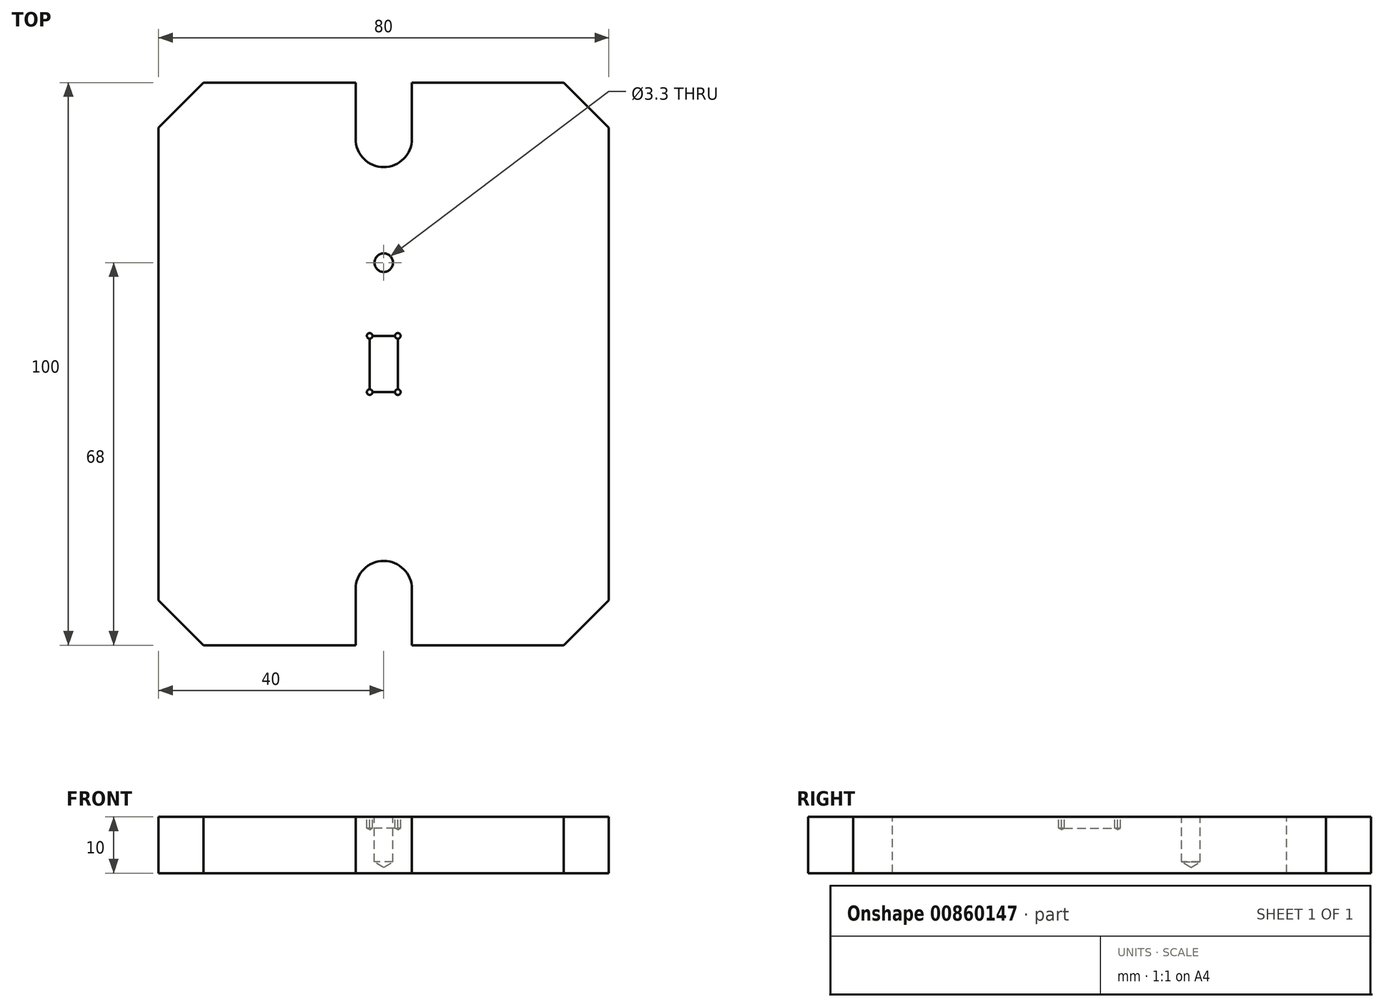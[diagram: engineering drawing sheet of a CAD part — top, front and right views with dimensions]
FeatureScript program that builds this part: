
annotation { "Feature Type Name" : "Feature", "Feature Type Description" : "" }
export const myFeature = defineFeature(function(context is Context, id is Id, definition is map)
    precondition{}
    {
        {
            var Q0;
            Q0=qCreatedBy(makeId("Top.planeOp"),FACE);
            var sketch = newSketch(context, id + "F0", { "sketchPlane" : qUnion([Q0])});
            skLineSegment(sketch, "E0.bottom", {"start": v(40, -50) * mm, "end": v(5, -50) * mm});
            skLineSegment(sketch, "E0.top", {"start": v(40, 50) * mm, "end": v(5, 50) * mm});
            skLineSegment(sketch, "E0.left", {"start": v(40, -50) * mm, "end": v(40, 50) * mm});
            skLineSegment(sketch, "E0.right", {"start": v(-40, -50) * mm, "end": v(-40, 50) * mm});
            skPoint(sketch, "E0.middle", {"position": v(0, 0) * mm});
            skLineSegment(sketch, "E1.bottom", {"start": v(2.5, -5) * mm, "end": v(-2.5, -5) * mm});
            skLineSegment(sketch, "E1.top", {"start": v(2.5, 5) * mm, "end": v(-2.5, 5) * mm});
            skLineSegment(sketch, "E1.left", {"start": v(2.5, -5) * mm, "end": v(2.5, 5) * mm});
            skLineSegment(sketch, "E1.right", {"start": v(-2.5, -5) * mm, "end": v(-2.5, 5) * mm});
            skLineSegment(sketch, "E2", {"start": v(-5, 50) * mm, "end": v(-5, 40) * mm});
            skLineSegment(sketch, "E3", {"start": v(5, 50) * mm, "end": v(5, 40) * mm});
            skArc(sketch, "E4", {"start": v(-5, 40) * mm, "mid": v(0, 35) * mm, "end": v(5, 40) * mm});
            skLineSegment(sketch, "E5.MirrorCS", {"start": v(-5, -50) * mm, "end": v(-5, -40) * mm});
            skLineSegment(sketch, "E6.MirrorCS", {"start": v(5, -50) * mm, "end": v(5, -40) * mm});
            skArc(sketch, "E7.MirrorCS", {"start": v(-5, -40) * mm, "mid": v(0, -35) * mm, "end": v(5, -40) * mm});
            skLineSegment(sketch, "E8.trimOffspring", {"start": v(-5, 50) * mm, "end": v(-40, 50) * mm});
            skLineSegment(sketch, "E9.trimOffspring", {"start": v(-5, -50) * mm, "end": v(-40, -50) * mm});
            skSolve(sketch);
        }
        {
            var Q0;
            Q0 = qSketchRegion(id + "F0", true);
            var Q1;
            Q1=makeQuery(id+"F0.imprint","IMPRINT",FACE,{"disambiguationData":[TD([[makeQuery(id+"F0.imprint","IMPRINT",EDGE,{"derivedFrom":sQuery(id+"F0.wireOp",EDGE,"E1.bottom")}),-1.0]])]});
            extrude(context, id + "F1", {"entities" : qUnion([Q0, Q1]), "oppositeDirection" : true, "depth" : 10 * mm, "offsetDistance" : 25 * mm});
        }
        {
            var Q0;
            Q0=makeQuery(id+"F1.opExtrude","SWEPT_EDGE",EDGE,{"disambiguationData":[OSD([sQuery(id+"F0.wireOp",EDGE,"E0.right"),sQuery(id+"F0.wireOp",EDGE,"E9.trimOffspring")])]});
            var Q1;
            Q1=makeQuery(id+"F1.opExtrude","SWEPT_EDGE",EDGE,{"disambiguationData":[OSD([sQuery(id+"F0.wireOp",EDGE,"E0.bottom"),sQuery(id+"F0.wireOp",EDGE,"E0.left")])]});
            var Q2;
            Q2=makeQuery(id+"F1.opExtrude","SWEPT_EDGE",EDGE,{"disambiguationData":[OSD([sQuery(id+"F0.wireOp",EDGE,"E0.right"),sQuery(id+"F0.wireOp",EDGE,"E8.trimOffspring")])]});
            var Q3;
            Q3=makeQuery(id+"F1.opExtrude","SWEPT_EDGE",EDGE,{"disambiguationData":[OSD([sQuery(id+"F0.wireOp",EDGE,"E0.top"),sQuery(id+"F0.wireOp",EDGE,"E0.left")])]});
            chamfer(context, id + "F2", {"entities" : qUnion([Q0, Q1, Q2, Q3]), "width" : 8 * mm, "tangentPropagation" : true});
        }
        {
            var Q0;
            Q0=makeQuery(id+"F0.imprint","IMPRINT",FACE,{"disambiguationData":[TD([[makeQuery(id+"F0.imprint","IMPRINT",EDGE,{"derivedFrom":sQuery(id+"F0.wireOp",EDGE,"E1.bottom")}),-1.0]])]});
            extrude(context, id + "F3", {"entities" : qUnion([Q0]), "operationType" : NewBodyOperationType.REMOVE, "oppositeDirection" : true, "depth" : 2 * mm, "offsetDistance" : 25 * mm});
        }
        {
            var Q0;
            Q0=sQuery(id+"F0.wireOp",VERTEX,"E1.top.end");
            var Q1;
            Q1=sQuery(id+"F0.wireOp",VERTEX,"E1.top.start");
            var Q2;
            Q2=sQuery(id+"F0.wireOp",VERTEX,"E1.bottom.end");
            var Q3;
            Q3=sQuery(id+"F0.wireOp",VERTEX,"E1.bottom.start");
            var Q4;
            Q4=makeQuery(id+"F1.opExtrude","SWEPT_BODY",BODY,{"disambiguationData":[OSD([sQuery(id+"F0.wireOp",EDGE,"E0.bottom"),sQuery(id+"F0.wireOp",EDGE,"E0.top"),sQuery(id+"F0.wireOp",EDGE,"E0.left"),sQuery(id+"F0.wireOp",EDGE,"E0.right"),sQuery(id+"F0.wireOp",EDGE,"E2"),sQuery(id+"F0.wireOp",EDGE,"E3"),sQuery(id+"F0.wireOp",EDGE,"E4"),sQuery(id+"F0.wireOp",EDGE,"E5.MirrorCS"),sQuery(id+"F0.wireOp",EDGE,"E6.MirrorCS"),sQuery(id+"F0.wireOp",EDGE,"E7.MirrorCS"),sQuery(id+"F0.wireOp",EDGE,"E8.trimOffspring"),sQuery(id+"F0.wireOp",EDGE,"E9.trimOffspring")])]});
            hole(context, id + "F4", {"style" : HoleStyle.SIMPLE, "endStyle" : HoleEndStyle.BLIND, "holeDiameter" : 1 * mm, "majorDiameter" : 5 * mm, "holeDepth" : 2 * mm, "isTappedThrough" : true, "tappedDepth" : 5.6 * mm, "tapClearance" : 3, "startFromSketch" : true, "locations" : qUnion([Q0, Q1, Q2, Q3]), "scope" : qUnion([Q4])});
        }
        {
            var Q0;
            Q0=makeQuery(id+"F1.opExtrude","CAP_FACE",FACE,{"disambiguationData":[OSD([sQuery(id+"F0.wireOp",EDGE,"E0.bottom"),sQuery(id+"F0.wireOp",EDGE,"E0.top"),sQuery(id+"F0.wireOp",EDGE,"E0.left"),sQuery(id+"F0.wireOp",EDGE,"E0.right"),sQuery(id+"F0.wireOp",EDGE,"E2"),sQuery(id+"F0.wireOp",EDGE,"E3"),sQuery(id+"F0.wireOp",EDGE,"E4"),sQuery(id+"F0.wireOp",EDGE,"E5.MirrorCS"),sQuery(id+"F0.wireOp",EDGE,"E6.MirrorCS"),sQuery(id+"F0.wireOp",EDGE,"E7.MirrorCS"),sQuery(id+"F0.wireOp",EDGE,"E8.trimOffspring"),sQuery(id+"F0.wireOp",EDGE,"E9.trimOffspring")])],"isStart":true});
            var sketch = newSketch(context, id + "F5", { "sketchPlane" : qUnion([Q0])});
            skPoint(sketch, "E10", {"position": v(0, 18) * mm});
            skSolve(sketch);
        }
        {
            var Q0;
            Q0=sQuery(id+"F5.wireOp",VERTEX,"E10");
            var Q1;
            Q1=makeQuery(id+"F1.opExtrude","SWEPT_BODY",BODY,{"disambiguationData":[OSD([sQuery(id+"F0.wireOp",EDGE,"E0.bottom"),sQuery(id+"F0.wireOp",EDGE,"E0.top"),sQuery(id+"F0.wireOp",EDGE,"E0.left"),sQuery(id+"F0.wireOp",EDGE,"E0.right"),sQuery(id+"F0.wireOp",EDGE,"E2"),sQuery(id+"F0.wireOp",EDGE,"E3"),sQuery(id+"F0.wireOp",EDGE,"E4"),sQuery(id+"F0.wireOp",EDGE,"E5.MirrorCS"),sQuery(id+"F0.wireOp",EDGE,"E6.MirrorCS"),sQuery(id+"F0.wireOp",EDGE,"E7.MirrorCS"),sQuery(id+"F0.wireOp",EDGE,"E8.trimOffspring"),sQuery(id+"F0.wireOp",EDGE,"E9.trimOffspring")])]});
            hole(context, id + "F6", {"style" : HoleStyle.SIMPLE, "endStyle" : HoleEndStyle.BLIND, "standardTappedOrClearance" : lookupTablePath({ "standard" : "ISO", "engagement" : "75%", "pitch" : "0.7 mm", "size" : "M4", "type" : "Tapped" }), "standardBlindInLast" : lookupTablePath({ "standard" : "ISO", "engagement" : "75%", "pitch" : "0.7 mm", "size" : "M4", "type" : "Tapped" }), "holeDiameter" : 3.3 * mm, "majorDiameter" : 4 * mm, "showTappedDepth" : true, "holeDepth" : 8 * mm, "isTappedThrough" : true, "tappedDepth" : 8 * mm, "tapClearance" : 0, "startFromSketch" : true, "locations" : qUnion([Q0]), "scope" : qUnion([Q1])});
        }
        {
            var Q0;
            Q0=qCreatedBy(makeId("Front.planeOp"),FACE);
            var sketch = newSketch(context, id + "F7", { "sketchPlane" : qUnion([Q0])});
            skLineSegment(sketch, "E11", {"start": v(0, 0) * mm, "end": v(0, 40) * mm});
            skSolve(sketch);
        }
    });
